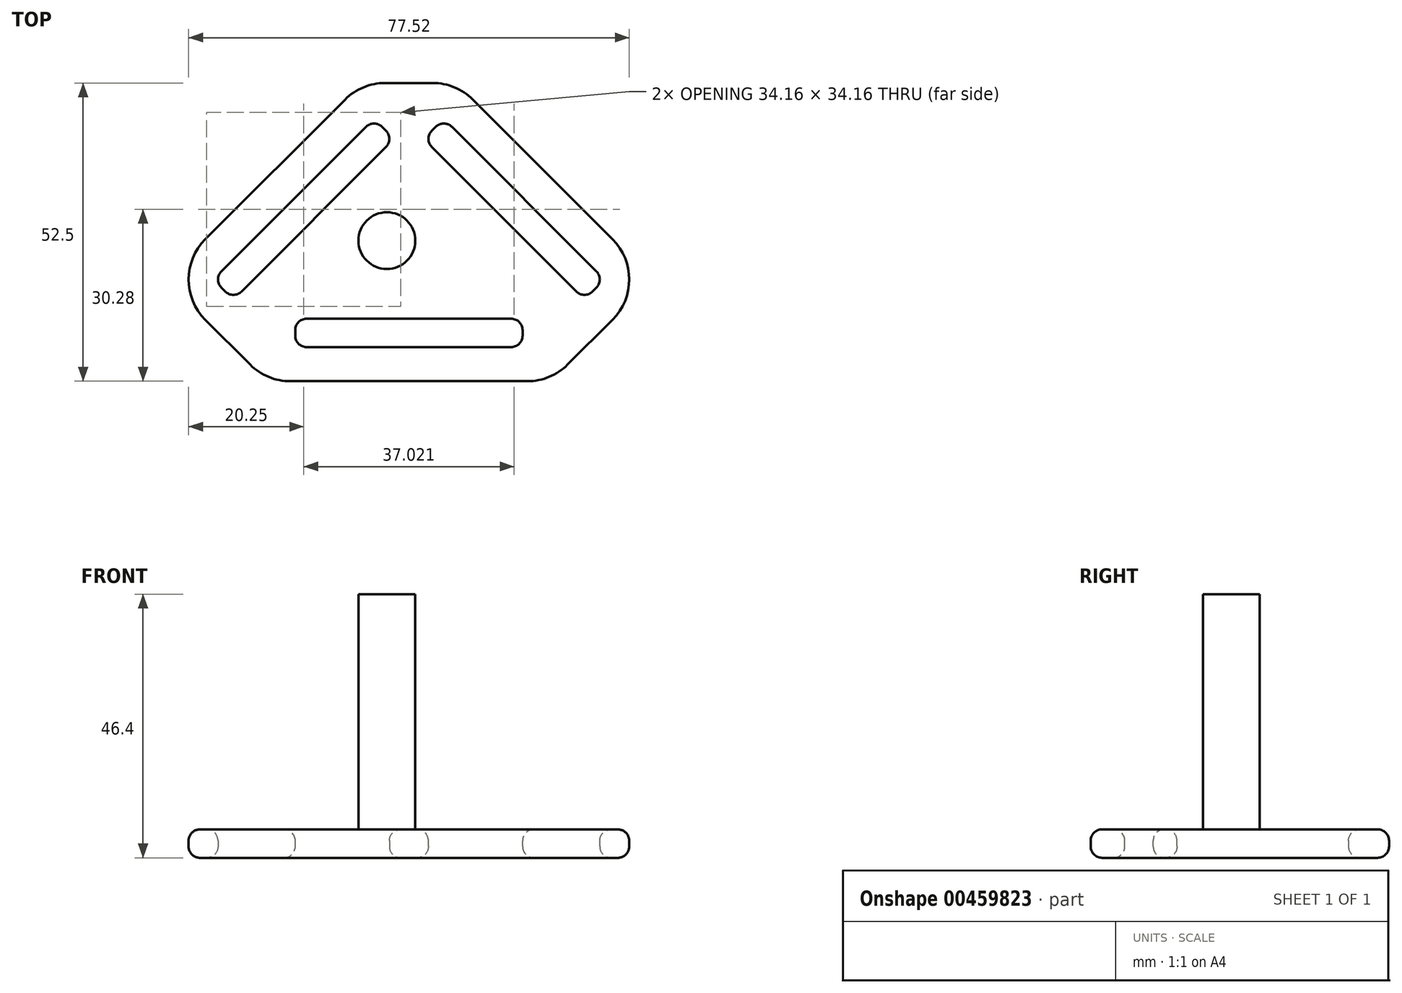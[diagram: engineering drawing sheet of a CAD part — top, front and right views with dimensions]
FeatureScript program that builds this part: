
annotation { "Feature Type Name" : "Feature", "Feature Type Description" : "" }
export const myFeature = defineFeature(function(context is Context, id is Id, definition is map)
    precondition{}
    {
        {
            var Q0;
            Q0=qCreatedBy(makeId("Top.planeOp"),FACE);
            var sketch = newSketch(context, id + "F0", { "sketchPlane" : qUnion([Q0])});
            skLineSegment(sketch, "E0", {"start": v(-60.81, 0) * mm, "end": v(60.81, 0) * mm, "construction": true});
            skLineSegment(sketch, "E1", {"start": v(-60.81, 0) * mm, "end": v(0, 60.81) * mm, "construction": true});
            skLineSegment(sketch, "E2", {"start": v(0, 60.81) * mm, "end": v(60.81, 0) * mm, "construction": true});
            skLineSegment(sketch, "E3", {"start": v(-8.31, 52.5) * mm, "end": v(8.31, 52.5) * mm});
            skLineSegment(sketch, "E4", {"start": v(-42.9, 17.9) * mm, "end": v(-25, 0) * mm});
            skLineSegment(sketch, "E5", {"start": v(42.9, 17.9) * mm, "end": v(25, 0) * mm});
            skPoint(sketch, "E6", {"position": v(-25, 0) * mm});
            skPoint(sketch, "E7", {"position": v(25, 0) * mm});
            skLineSegment(sketch, "E8", {"start": v(-42.9, 17.9) * mm, "end": v(-8.31, 52.5) * mm});
            skLineSegment(sketch, "E9", {"start": v(8.31, 52.5) * mm, "end": v(42.9, 17.9) * mm});
            skLineSegment(sketch, "E10", {"start": v(25, 0) * mm, "end": v(-25, 0) * mm});
            skSolve(sketch);
        }
        {
            var Q0;
            Q0=qSketchRegion(id+"F0",true);
            extrude(context, id + "F1", {"entities" : qUnion([Q0]), "depth" : 5 * mm});
        }
        {
            var Q0;
            Q0=makeQuery(id+"F1.opExtrude","CAP_FACE",FACE,{"disambiguationData":[OSD([sQuery(id+"F0.wireOp",EDGE,"E3"),sQuery(id+"F0.wireOp",EDGE,"E4"),sQuery(id+"F0.wireOp",EDGE,"E5"),sQuery(id+"F0.wireOp",EDGE,"E8"),sQuery(id+"F0.wireOp",EDGE,"E9"),sQuery(id+"F0.wireOp",EDGE,"E10")])],"isStart":false});
            var sketch = newSketch(context, id + "F2", { "sketchPlane" : qUnion([Q0])});
            skPoint(sketch, "E11.orphan", {"position": v(-0.64, 59.84) * mm});
            skLineSegment(sketch, "E12.bottom", {"start": v(-20, 6) * mm, "end": v(20, 6) * mm});
            skLineSegment(sketch, "E12.top", {"start": v(-20, 11) * mm, "end": v(20, 11) * mm});
            skLineSegment(sketch, "E12.left", {"start": v(-20, 6) * mm, "end": v(-20, 11) * mm});
            skLineSegment(sketch, "E12.right", {"start": v(20, 6) * mm, "end": v(20, 11) * mm});
            skLineSegment(sketch, "E13.bottom", {"start": v(-30.88, 14.37) * mm, "end": v(-2.6, 42.65) * mm});
            skLineSegment(sketch, "E13.top", {"start": v(-34.42, 17.9) * mm, "end": v(-6.14, 46.19) * mm});
            skLineSegment(sketch, "E13.left", {"start": v(-30.88, 14.37) * mm, "end": v(-34.42, 17.9) * mm});
            skLineSegment(sketch, "E13.right", {"start": v(-2.6, 42.65) * mm, "end": v(-6.14, 46.19) * mm});
            skLineSegment(sketch, "E14.bottom", {"start": v(2.6, 42.65) * mm, "end": v(6.14, 46.19) * mm});
            skLineSegment(sketch, "E14.top", {"start": v(30.88, 14.37) * mm, "end": v(34.42, 17.9) * mm});
            skLineSegment(sketch, "E14.left", {"start": v(2.6, 42.65) * mm, "end": v(30.88, 14.37) * mm});
            skLineSegment(sketch, "E14.right", {"start": v(6.14, 46.19) * mm, "end": v(34.42, 17.9) * mm});
            skSolve(sketch);
        }
        {
            var Q0;
            Q0=qSketchRegion(id+"F2",true);
            extrude(context, id + "F3", {"entities" : qUnion([Q0]), "operationType" : NewBodyOperationType.REMOVE, "oppositeDirection" : true, "depth" : 25 * mm});
        }
        {
            var Q0;
            Q0=makeQuery(id+"F1.opExtrude","SWEPT_EDGE",EDGE,{"disambiguationData":[OSD([sQuery(id+"F0.wireOp",EDGE,"E4"),sQuery(id+"F0.wireOp",EDGE,"E8")])]});
            var Q1;
            Q1=makeQuery(id+"F1.opExtrude","SWEPT_EDGE",EDGE,{"disambiguationData":[OSD([sQuery(id+"F0.wireOp",EDGE,"E5"),sQuery(id+"F0.wireOp",EDGE,"E9")])]});
            var Q2;
            Q2=makeQuery(id+"F1.opExtrude","SWEPT_EDGE",EDGE,{"disambiguationData":[OSD([sQuery(id+"F0.wireOp",EDGE,"E5"),sQuery(id+"F0.wireOp",EDGE,"E10")])]});
            var Q3;
            Q3=makeQuery(id+"F1.opExtrude","SWEPT_EDGE",EDGE,{"disambiguationData":[OSD([sQuery(id+"F0.wireOp",EDGE,"E4"),sQuery(id+"F0.wireOp",EDGE,"E10")])]});
            var Q4;
            Q4=makeQuery(id+"F1.opExtrude","SWEPT_EDGE",EDGE,{"disambiguationData":[OSD([sQuery(id+"F0.wireOp",EDGE,"E3"),sQuery(id+"F0.wireOp",EDGE,"E9")])]});
            var Q5;
            Q5=makeQuery(id+"F1.opExtrude","SWEPT_EDGE",EDGE,{"disambiguationData":[OSD([sQuery(id+"F0.wireOp",EDGE,"E3"),sQuery(id+"F0.wireOp",EDGE,"E8")])]});
            fillet(context, id + "F4", {"entities" : qUnion([Q0, Q1, Q2, Q3, Q4, Q5]), "radius" : 10 * mm, "tangentPropagation" : true, "allowEdgeOverflow" : false});
        }
        {
            var Q0;
            Q0=makeQuery(id+"F3.boolean.opBoolean","COPY",EDGE,{"derivedFrom":makeQuery(id+"F3.opExtrude","SWEPT_EDGE",EDGE,{"disambiguationData":[OSD([sQuery(id+"F2.wireOp",EDGE,"E13.top"),sQuery(id+"F2.wireOp",EDGE,"E13.right")])]})});
            var Q1;
            Q1=makeQuery(id+"F3.boolean.opBoolean","COPY",EDGE,{"derivedFrom":makeQuery(id+"F3.opExtrude","SWEPT_EDGE",EDGE,{"disambiguationData":[OSD([sQuery(id+"F2.wireOp",EDGE,"E14.bottom"),sQuery(id+"F2.wireOp",EDGE,"E14.right")])]})});
            var Q2;
            Q2=makeQuery(id+"F3.boolean.opBoolean","COPY",EDGE,{"derivedFrom":makeQuery(id+"F3.opExtrude","SWEPT_EDGE",EDGE,{"disambiguationData":[OSD([sQuery(id+"F2.wireOp",EDGE,"E13.bottom"),sQuery(id+"F2.wireOp",EDGE,"E13.right")])]})});
            var Q3;
            Q3=makeQuery(id+"F3.boolean.opBoolean","COPY",EDGE,{"derivedFrom":makeQuery(id+"F3.opExtrude","SWEPT_EDGE",EDGE,{"disambiguationData":[OSD([sQuery(id+"F2.wireOp",EDGE,"E14.top"),sQuery(id+"F2.wireOp",EDGE,"E14.right")])]})});
            var Q4;
            Q4=makeQuery(id+"F3.boolean.opBoolean","COPY",EDGE,{"derivedFrom":makeQuery(id+"F3.opExtrude","SWEPT_EDGE",EDGE,{"disambiguationData":[OSD([sQuery(id+"F2.wireOp",EDGE,"E12.top"),sQuery(id+"F2.wireOp",EDGE,"E12.right")])]})});
            var Q5;
            Q5=makeQuery(id+"F3.boolean.opBoolean","COPY",EDGE,{"derivedFrom":makeQuery(id+"F3.opExtrude","SWEPT_EDGE",EDGE,{"disambiguationData":[OSD([sQuery(id+"F2.wireOp",EDGE,"E13.top"),sQuery(id+"F2.wireOp",EDGE,"E13.left")])]})});
            var Q6;
            Q6=makeQuery(id+"F3.boolean.opBoolean","COPY",EDGE,{"derivedFrom":makeQuery(id+"F3.opExtrude","SWEPT_EDGE",EDGE,{"disambiguationData":[OSD([sQuery(id+"F2.wireOp",EDGE,"E12.top"),sQuery(id+"F2.wireOp",EDGE,"E12.left")])]})});
            var Q7;
            Q7=makeQuery(id+"F3.boolean.opBoolean","COPY",EDGE,{"derivedFrom":makeQuery(id+"F3.opExtrude","SWEPT_EDGE",EDGE,{"disambiguationData":[OSD([sQuery(id+"F2.wireOp",EDGE,"E12.bottom"),sQuery(id+"F2.wireOp",EDGE,"E12.left")])]})});
            var Q8;
            Q8=makeQuery(id+"F3.boolean.opBoolean","COPY",EDGE,{"derivedFrom":makeQuery(id+"F3.opExtrude","SWEPT_EDGE",EDGE,{"disambiguationData":[OSD([sQuery(id+"F2.wireOp",EDGE,"E12.bottom"),sQuery(id+"F2.wireOp",EDGE,"E12.right")])]})});
            var Q9;
            Q9=makeQuery(id+"F3.boolean.opBoolean","COPY",EDGE,{"derivedFrom":makeQuery(id+"F3.opExtrude","SWEPT_EDGE",EDGE,{"disambiguationData":[OSD([sQuery(id+"F2.wireOp",EDGE,"E14.top"),sQuery(id+"F2.wireOp",EDGE,"E14.left")])]})});
            var Q10;
            Q10=makeQuery(id+"F3.boolean.opBoolean","COPY",EDGE,{"derivedFrom":makeQuery(id+"F3.opExtrude","SWEPT_EDGE",EDGE,{"disambiguationData":[OSD([sQuery(id+"F2.wireOp",EDGE,"E13.bottom"),sQuery(id+"F2.wireOp",EDGE,"E13.left")])]})});
            var Q11;
            Q11=makeQuery(id+"F3.boolean.opBoolean","COPY",EDGE,{"derivedFrom":makeQuery(id+"F3.opExtrude","SWEPT_EDGE",EDGE,{"disambiguationData":[OSD([sQuery(id+"F2.wireOp",EDGE,"E14.bottom"),sQuery(id+"F2.wireOp",EDGE,"E14.left")])]})});
            fillet(context, id + "F5", {"entities" : qUnion([Q0, Q1, Q2, Q3, Q4, Q5, Q6, Q7, Q8, Q9, Q10, Q11]), "radius" : 2 * mm, "tangentPropagation" : true, "allowEdgeOverflow" : false});
        }
        {
            var Q0;
            Q0=makeQuery(id+"F1.opExtrude","CAP_FACE",FACE,{"disambiguationData":[OSD([sQuery(id+"F0.wireOp",EDGE,"E3"),sQuery(id+"F0.wireOp",EDGE,"E4"),sQuery(id+"F0.wireOp",EDGE,"E5"),sQuery(id+"F0.wireOp",EDGE,"E8"),sQuery(id+"F0.wireOp",EDGE,"E9"),sQuery(id+"F0.wireOp",EDGE,"E10")])],"isStart":false});
            var Q1;
            Q1=makeQuery(id+"F1.opExtrude","CAP_FACE",FACE,{"disambiguationData":[OSD([sQuery(id+"F0.wireOp",EDGE,"E3"),sQuery(id+"F0.wireOp",EDGE,"E4"),sQuery(id+"F0.wireOp",EDGE,"E5"),sQuery(id+"F0.wireOp",EDGE,"E8"),sQuery(id+"F0.wireOp",EDGE,"E9"),sQuery(id+"F0.wireOp",EDGE,"E10")])],"isStart":true});
            fillet(context, id + "F6", {"entities" : qUnion([Q0, Q1]), "radius" : 2 * mm, "tangentPropagation" : true, "allowEdgeOverflow" : false});
        }
        {
            var Q0;
            Q0=makeQuery(id+"F1.opExtrude","CAP_FACE",FACE,{"disambiguationData":[OSD([sQuery(id+"F0.wireOp",EDGE,"E3"),sQuery(id+"F0.wireOp",EDGE,"E4"),sQuery(id+"F0.wireOp",EDGE,"E5"),sQuery(id+"F0.wireOp",EDGE,"E8"),sQuery(id+"F0.wireOp",EDGE,"E9"),sQuery(id+"F0.wireOp",EDGE,"E10")])],"isStart":false});
            var sketch = newSketch(context, id + "F7", { "sketchPlane" : qUnion([Q0])});
            skCircle(sketch, "E15", {"center": v(-3.87, 24.74) * mm, "radius": 5 * mm});
            skSolve(sketch);
        }
        {
            var Q0;
            Q0 = qSketchRegion(id + "F7", true);
            extrude(context, id + "F8", {"entities" : qUnion([Q0]), "operationType" : NewBodyOperationType.ADD, "depth" : 41.4 * mm});
        }
    });
